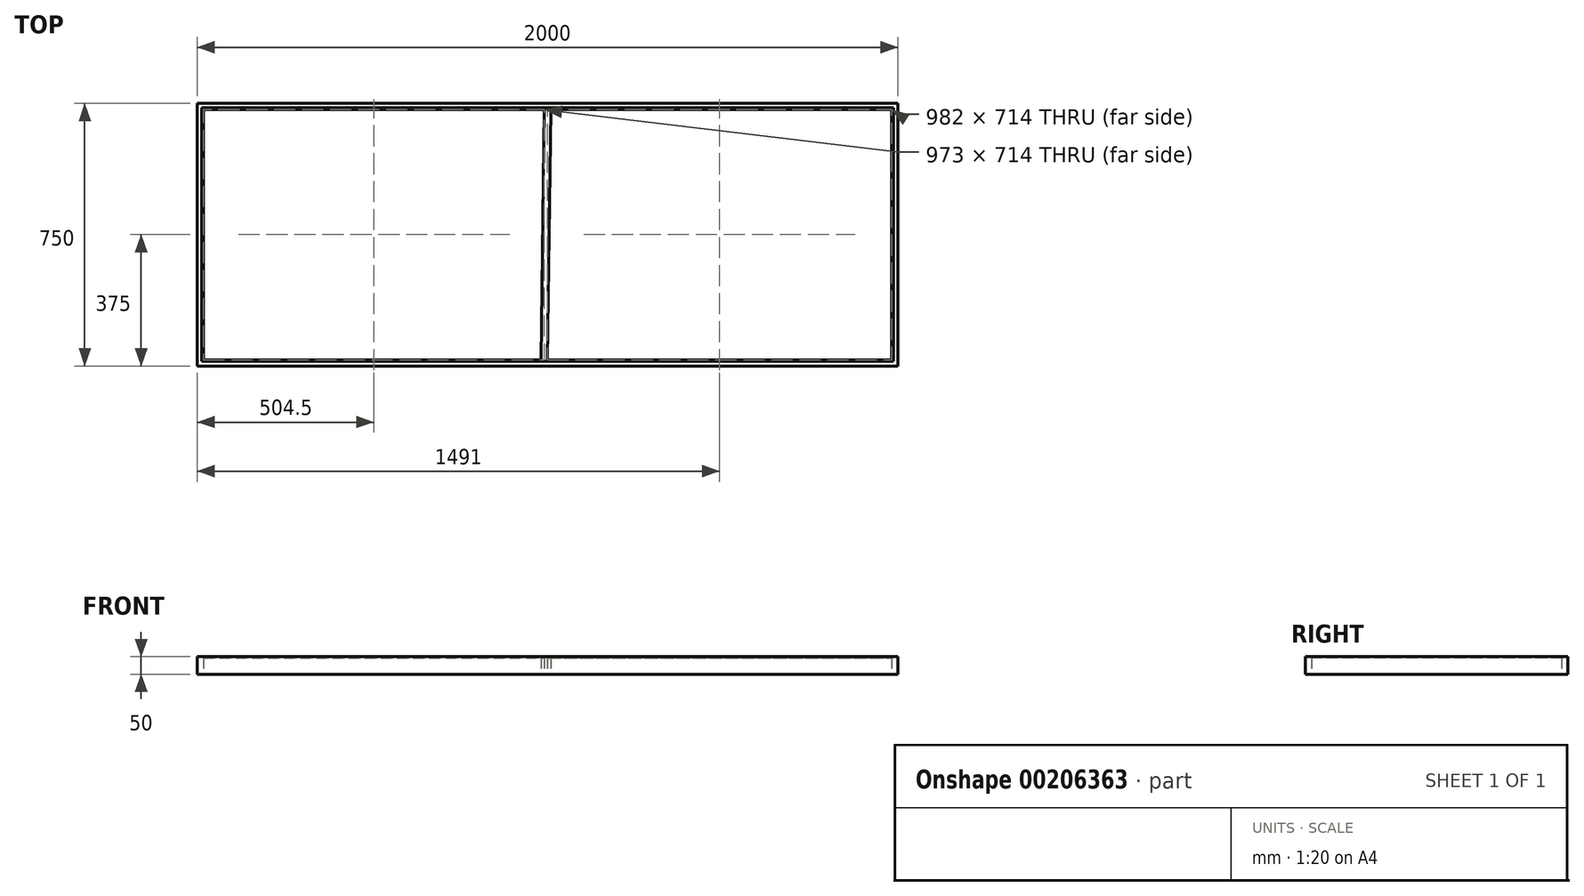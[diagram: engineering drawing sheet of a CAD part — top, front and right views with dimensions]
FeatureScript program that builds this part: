
annotation { "Feature Type Name" : "Feature", "Feature Type Description" : "" }
export const myFeature = defineFeature(function(context is Context, id is Id, definition is map)
    precondition{}
    {
        {
            var Q0;
            Q0=qCreatedBy(makeId("Top.planeOp"),FACE);
            var sketch = newSketch(context, id + "F0", { "sketchPlane" : qUnion([Q0])});
            skLineSegment(sketch, "E0.bottom", {"start": v(-1000, 375) * mm, "end": v(1000, 375) * mm});
            skLineSegment(sketch, "E0.top", {"start": v(-1000, -375) * mm, "end": v(1000, -375) * mm});
            skLineSegment(sketch, "E0.left", {"start": v(-1000, 375) * mm, "end": v(-1000, -375) * mm});
            skLineSegment(sketch, "E0.right", {"start": v(1000, 375) * mm, "end": v(1000, -375) * mm});
            skPoint(sketch, "E0.middle", {"position": v(0, 0) * mm});
            skSolve(sketch);
        }
        {
            var Q0;
            Q0=makeQuery(id+"F0.imprint","IMPRINT",FACE,{"disambiguationData":[TD([[makeQuery(id+"F0.imprint","IMPRINT",EDGE,{"derivedFrom":sQuery(id+"F0.wireOp",EDGE,"E0.bottom")}),-1.0]])]});
            extrude(context, id + "F1", {"entities" : qUnion([Q0]), "depth" : 50 * mm});
        }
        {
            var Q0;
            Q0=makeQuery(id+"F1.opExtrude","CAP_FACE",FACE,{"disambiguationData":[OSD([sQuery(id+"F0.wireOp",EDGE,"E0.bottom"),sQuery(id+"F0.wireOp",EDGE,"E0.top"),sQuery(id+"F0.wireOp",EDGE,"E0.left"),sQuery(id+"F0.wireOp",EDGE,"E0.right")])],"isStart":false});
            shell(context, id + "F2", {"entities" : qUnion([Q0]), "thickness" : 18 * mm});
        }
        {
            var Q0;
            Q0=makeQuery(id+"F2.opShell","OFFSET_FACE",FACE,{"disambiguationData":[OSD([sQuery(id+"F0.wireOp",EDGE,"E0.bottom"),sQuery(id+"F0.wireOp",EDGE,"E0.top"),sQuery(id+"F0.wireOp",EDGE,"E0.left"),sQuery(id+"F0.wireOp",EDGE,"E0.right")])]});
            extrude(context, id + "F3", {"entities" : qUnion([Q0]), "operationType" : NewBodyOperationType.REMOVE, "oppositeDirection" : true, "depth" : 25 * mm});
        }
        {
            var Q0;
            Q0=makeQuery(id+"F0.imprint","IMPRINT",FACE,{"disambiguationData":[TD([[makeQuery(id+"F0.imprint","IMPRINT",EDGE,{"derivedFrom":sQuery(id+"F0.wireOp",EDGE,"E0.bottom")}),-1.0]])]});
            var sketch = newSketch(context, id + "F4", { "sketchPlane" : qUnion([Q0])});
            skLineSegment(sketch, "E1", {"start": v(0, 357) * mm, "end": v(-9, 357) * mm});
            skLineSegment(sketch, "E2", {"start": v(-9, 357) * mm, "end": v(9, 357) * mm});
            skLineSegment(sketch, "E3", {"start": v(9, 357) * mm, "end": v(0, -357) * mm});
            skLineSegment(sketch, "E4", {"start": v(0, -357) * mm, "end": v(-18, -357) * mm});
            skLineSegment(sketch, "E5", {"start": v(-18, -357) * mm, "end": v(-9, 357) * mm});
            skSolve(sketch);
        }
        {
            var Q0;
            {var subQ0=sQuery(id+"F4.wireOp",EDGE,"E3");Q0=makeQuery(id+"F4.imprint","IMPRINT",FACE,{"disambiguationData":[TD([[makeQuery(id+"F4.imprint","IMPRINT",EDGE,{"derivedFrom":subQ0}),-1.0]])]});}
            extrude(context, id + "F5", {"entities" : qUnion([Q0]), "operationType" : NewBodyOperationType.ADD, "depth" : 46.5 * mm});
        }
        {
            var Q0;
            Q0=makeQuery(id+"F1.opExtrude","CAP_FACE",FACE,{"disambiguationData":[OSD([sQuery(id+"F0.wireOp",EDGE,"E0.bottom"),sQuery(id+"F0.wireOp",EDGE,"E0.top"),sQuery(id+"F0.wireOp",EDGE,"E0.left"),sQuery(id+"F0.wireOp",EDGE,"E0.right")])],"isStart":false});
            var sketch = newSketch(context, id + "F6", { "sketchPlane" : qUnion([Q0])});
            skLineSegment(sketch, "E6", {"start": v(-982, 362) * mm, "end": v(982, 362) * mm});
            skLineSegment(sketch, "E7", {"start": v(987, 357) * mm, "end": v(987, -357) * mm});
            skLineSegment(sketch, "E8", {"start": v(982, -362) * mm, "end": v(-987, -362) * mm});
            skLineSegment(sketch, "E9", {"start": v(-987, -362) * mm, "end": v(-982, -362) * mm});
            skLineSegment(sketch, "E10", {"start": v(-987, -357) * mm, "end": v(-987, -362) * mm});
            skLineSegment(sketch, "E11", {"start": v(-987, -357) * mm, "end": v(-987, 357) * mm});
            skLineSegment(sketch, "E12", {"start": v(-982, 362) * mm, "end": v(-987, 362) * mm});
            skLineSegment(sketch, "E13", {"start": v(-987, 362) * mm, "end": v(-987, 357) * mm});
            skLineSegment(sketch, "E14", {"start": v(982, 362) * mm, "end": v(987, 362) * mm});
            skLineSegment(sketch, "E15", {"start": v(987, 362) * mm, "end": v(987, 357) * mm});
            skLineSegment(sketch, "E16", {"start": v(987, -357) * mm, "end": v(987, -362) * mm});
            skLineSegment(sketch, "E17", {"start": v(987, -362) * mm, "end": v(982, -362) * mm});
            skLineSegment(sketch, "E18.top", {"start": v(-982, 362) * mm, "end": v(987, 362) * mm});
            skLineSegment(sketch, "E18.right", {"start": v(987, -357) * mm, "end": v(987, 362) * mm});
            skSolve(sketch);
        }
        {
            var Q0;
            Q0=makeQuery(id+"F6.imprint","IMPRINT",FACE,{"disambiguationData":[TD([[makeQuery(id+"F6.imprint","IMPRINT",EDGE,{"derivedFrom":sQuery(id+"F6.wireOp",EDGE,"E8")}),-1.0]])]});
            extrude(context, id + "F7", {"entities" : qUnion([Q0]), "operationType" : NewBodyOperationType.REMOVE, "oppositeDirection" : true, "depth" : 3.5 * mm});
        }
    });
